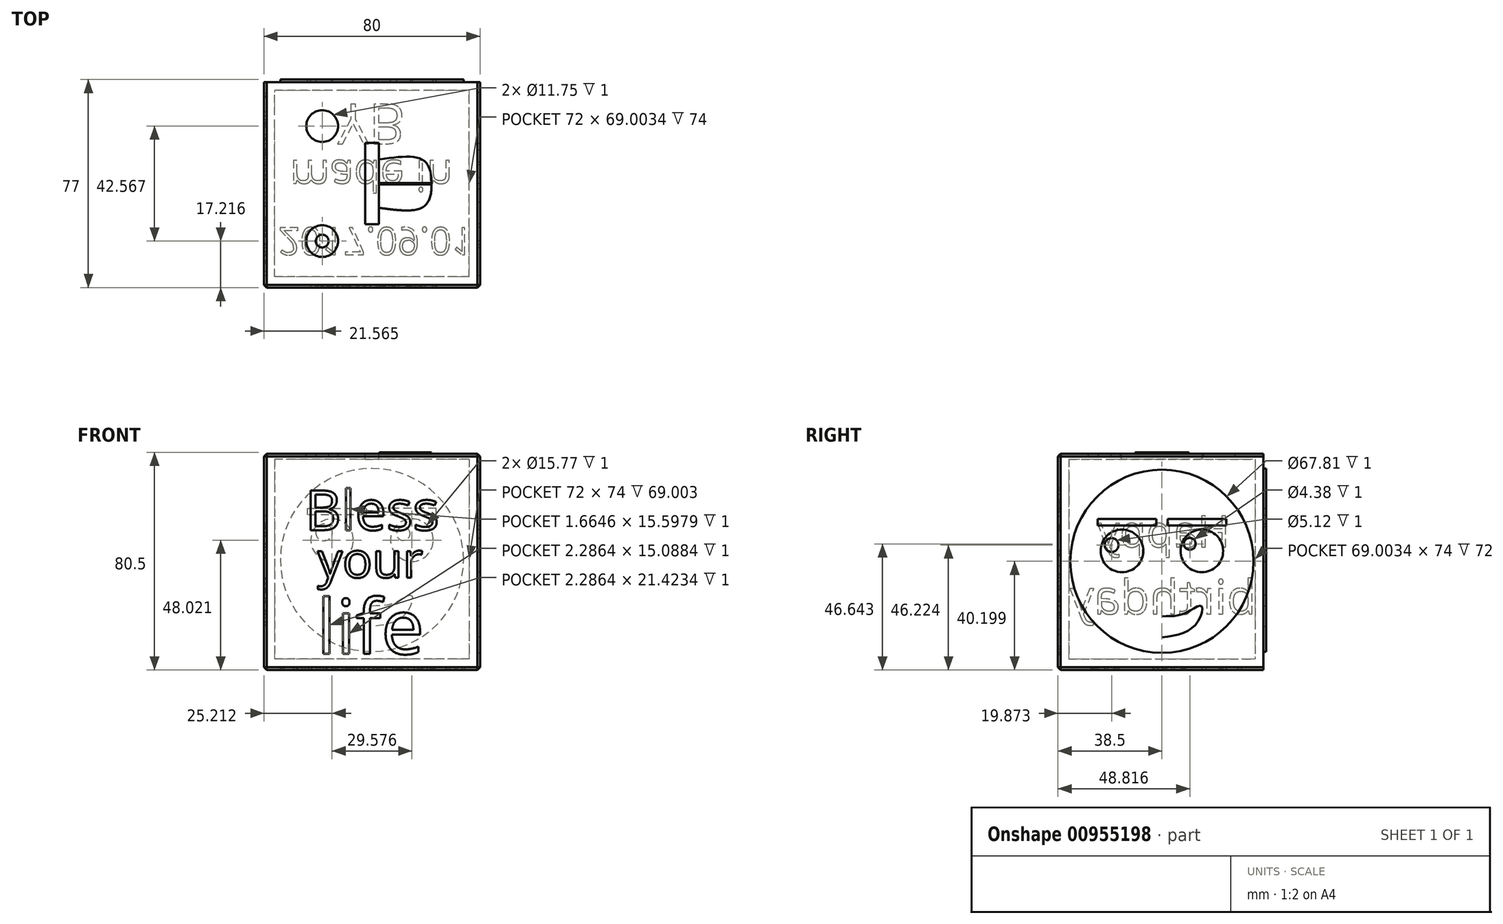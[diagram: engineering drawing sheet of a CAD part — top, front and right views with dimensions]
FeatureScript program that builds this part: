
annotation { "Feature Type Name" : "Feature", "Feature Type Description" : "" }
export const myFeature = defineFeature(function(context is Context, id is Id, definition is map)
    precondition{}
    {
        {
            var Q0;
            Q0=qCreatedBy(makeId("Top.planeOp"),FACE);
            var sketch = newSketch(context, id + "F0", { "sketchPlane" : qUnion([Q0])});
            skLineSegment(sketch, "E0.bottom", {"start": v(40, -38.5) * mm, "end": v(-40, -38.5) * mm});
            skLineSegment(sketch, "E0.top", {"start": v(40, 38.5) * mm, "end": v(-40, 38.5) * mm});
            skLineSegment(sketch, "E0.left", {"start": v(40, -38.5) * mm, "end": v(40, 38.5) * mm});
            skLineSegment(sketch, "E0.right", {"start": v(-40, -38.5) * mm, "end": v(-40, 38.5) * mm});
            skPoint(sketch, "E0.middle", {"position": v(0, 0) * mm});
            skSolve(sketch);
        }
        {
            var Q0;
            Q0 = qSketchRegion(id + "F0", true);
            extrude(context, id + "F1", {"entities" : qUnion([Q0]), "depth" : 78 * mm, "offsetDistance" : 25.4 * mm});
        }
        {
            var Q0;
            Q0=makeQuery(id+"F1.opExtrude","CAP_FACE",FACE,{"disambiguationData":[OSD([sQuery(id+"F0.wireOp",EDGE,"E0.bottom"),sQuery(id+"F0.wireOp",EDGE,"E0.top"),sQuery(id+"F0.wireOp",EDGE,"E0.left"),sQuery(id+"F0.wireOp",EDGE,"E0.right")])],"isStart":false});
            shell(context, id + "F2", {"entities" : qUnion([Q0]), "thickness" : 4 * mm});
        }
        {
            var Q0;
            Q0=makeQuery(id+"F1.opExtrude","CAP_FACE",FACE,{"disambiguationData":[OSD([sQuery(id+"F0.wireOp",EDGE,"E0.bottom"),sQuery(id+"F0.wireOp",EDGE,"E0.top"),sQuery(id+"F0.wireOp",EDGE,"E0.left"),sQuery(id+"F0.wireOp",EDGE,"E0.right")])],"isStart":false});
            var sketch = newSketch(context, id + "F3", { "sketchPlane" : qUnion([Q0])});
            skLineSegment(sketch, "E1.bottom", {"start": v(-40, 38.5) * mm, "end": v(40, 38.5) * mm});
            skLineSegment(sketch, "E1.top", {"start": v(-40, -38.5) * mm, "end": v(40, -38.5) * mm});
            skLineSegment(sketch, "E1.left", {"start": v(-40, 38.5) * mm, "end": v(-40, -38.5) * mm});
            skLineSegment(sketch, "E1.right", {"start": v(40, 38.5) * mm, "end": v(40, -38.5) * mm});
            skPoint(sketch, "E1.middle", {"position": v(0, 0) * mm});
            skSolve(sketch);
        }
        {
            var Q0;
            Q0 = qSketchRegion(id + "F3", true);
            extrude(context, id + "F4", {"entities" : qUnion([Q0]), "operationType" : NewBodyOperationType.ADD, "depth" : 2 * mm, "offsetDistance" : 25.4 * mm});
        }
        {
            var Q0;
            Q0=makeQuery(id+"F4.opExtrude","CAP_FACE",FACE,{"disambiguationData":[OSD([sQuery(id+"F3.wireOp",EDGE,"E1.bottom"),sQuery(id+"F3.wireOp",EDGE,"E1.top"),sQuery(id+"F3.wireOp",EDGE,"E1.left"),sQuery(id+"F3.wireOp",EDGE,"E1.right")])],"isStart":false});
            var sketch = newSketch(context, id + "F5", { "sketchPlane" : qUnion([Q0])});
            skLineSegment(sketch, "E2.bottom", {"start": v(-2.5, 15) * mm, "end": v(2.5, 15) * mm});
            skLineSegment(sketch, "E2.top", {"start": v(-2.5, -15) * mm, "end": v(2.5, -15) * mm});
            skLineSegment(sketch, "E2.left", {"start": v(-2.5, 15) * mm, "end": v(-2.5, -15) * mm});
            skLineSegment(sketch, "E2.right", {"start": v(2.5, 15) * mm, "end": v(2.5, -15) * mm});
            skPoint(sketch, "E2.middle", {"position": v(0, 0) * mm});
            skSolve(sketch);
        }
        {
            var Q0;
            Q0=makeQuery(id+"F5.imprint","IMPRINT",FACE,{"disambiguationData":[TD([[makeQuery(id+"F5.imprint","IMPRINT",EDGE,{"derivedFrom":sQuery(id+"F5.wireOp",EDGE,"E2.bottom")}),-1.0]])]});
            extrude(context, id + "F6", {"entities" : qUnion([Q0]), "operationType" : NewBodyOperationType.REMOVE, "oppositeDirection" : true, "depth" : 25.4 * mm, "offsetDistance" : 25.4 * mm});
        }
        {
            var Q0;
            Q0=makeQuery(id+"F4.opExtrude","CAP_EDGE",EDGE,{"disambiguationData":[OSD([sQuery(id+"F3.wireOp",EDGE,"E1.bottom")])],"isStart":false});
            var Q1;
            Q1=makeQuery(id+"F4.opExtrude","CAP_EDGE",EDGE,{"disambiguationData":[OSD([sQuery(id+"F3.wireOp",EDGE,"E1.right")])],"isStart":false});
            var Q2;
            Q2=makeQuery(id+"F4.boolean.opBoolean","MERGE",EDGE,{"derivedFrom":[makeQuery(id+"F1.opExtrude","SWEPT_EDGE",EDGE,{"disambiguationData":[OSD([sQuery(id+"F0.wireOp",EDGE,"E0.top"),sQuery(id+"F0.wireOp",EDGE,"E0.right")])]}),makeQuery(id+"F4.opExtrude","SWEPT_EDGE",EDGE,{"disambiguationData":[OSD([sQuery(id+"F3.wireOp",EDGE,"E1.bottom"),sQuery(id+"F3.wireOp",EDGE,"E1.left")])]})]});
            var Q3;
            Q3=makeQuery(id+"F4.opExtrude","CAP_EDGE",EDGE,{"disambiguationData":[OSD([sQuery(id+"F3.wireOp",EDGE,"E1.left")])],"isStart":false});
            var Q4;
            Q4=makeQuery(id+"F4.opExtrude","CAP_EDGE",EDGE,{"disambiguationData":[OSD([sQuery(id+"F3.wireOp",EDGE,"E1.top")])],"isStart":false});
            var Q5;
            Q5=makeQuery(id+"F4.boolean.opBoolean","MERGE",EDGE,{"derivedFrom":[makeQuery(id+"F1.opExtrude","SWEPT_EDGE",EDGE,{"disambiguationData":[OSD([sQuery(id+"F0.wireOp",EDGE,"E0.bottom"),sQuery(id+"F0.wireOp",EDGE,"E0.right")])]}),makeQuery(id+"F4.opExtrude","SWEPT_EDGE",EDGE,{"disambiguationData":[OSD([sQuery(id+"F3.wireOp",EDGE,"E1.top"),sQuery(id+"F3.wireOp",EDGE,"E1.left")])]})]});
            var Q6;
            Q6=makeQuery(id+"F1.opExtrude","CAP_EDGE",EDGE,{"disambiguationData":[OSD([sQuery(id+"F0.wireOp",EDGE,"E0.bottom")])],"isStart":true});
            var Q7;
            Q7=makeQuery(id+"F1.opExtrude","CAP_EDGE",EDGE,{"disambiguationData":[OSD([sQuery(id+"F0.wireOp",EDGE,"E0.right")])],"isStart":true});
            var Q8;
            Q8=makeQuery(id+"F4.boolean.opBoolean","MERGE",EDGE,{"derivedFrom":[makeQuery(id+"F1.opExtrude","SWEPT_EDGE",EDGE,{"disambiguationData":[OSD([sQuery(id+"F0.wireOp",EDGE,"E0.bottom"),sQuery(id+"F0.wireOp",EDGE,"E0.left")])]}),makeQuery(id+"F4.opExtrude","SWEPT_EDGE",EDGE,{"disambiguationData":[OSD([sQuery(id+"F3.wireOp",EDGE,"E1.top"),sQuery(id+"F3.wireOp",EDGE,"E1.right")])]})]});
            var Q9;
            Q9=makeQuery(id+"F4.boolean.opBoolean","MERGE",EDGE,{"derivedFrom":[makeQuery(id+"F1.opExtrude","SWEPT_EDGE",EDGE,{"disambiguationData":[OSD([sQuery(id+"F0.wireOp",EDGE,"E0.top"),sQuery(id+"F0.wireOp",EDGE,"E0.left")])]}),makeQuery(id+"F4.opExtrude","SWEPT_EDGE",EDGE,{"disambiguationData":[OSD([sQuery(id+"F3.wireOp",EDGE,"E1.bottom"),sQuery(id+"F3.wireOp",EDGE,"E1.right")])]})]});
            var Q10;
            Q10=makeQuery(id+"F1.opExtrude","CAP_EDGE",EDGE,{"disambiguationData":[OSD([sQuery(id+"F0.wireOp",EDGE,"E0.left")])],"isStart":true});
            var Q11;
            Q11=makeQuery(id+"F1.opExtrude","CAP_FACE",FACE,{"disambiguationData":[OSD([sQuery(id+"F0.wireOp",EDGE,"E0.bottom"),sQuery(id+"F0.wireOp",EDGE,"E0.top"),sQuery(id+"F0.wireOp",EDGE,"E0.left"),sQuery(id+"F0.wireOp",EDGE,"E0.right")])],"isStart":true});
            chamfer(context, id + "F7", {"entities" : qUnion([Q0, Q1, Q2, Q3, Q4, Q5, Q6, Q7, Q8, Q9, Q10, Q11]), "width" : 1 * mm, "tangentPropagation" : true});
        }
        {
            var Q0;
            Q0=makeQuery(id+"F4.boolean.opBoolean","MERGE",FACE,{"derivedFrom":[makeQuery(id+"F1.opExtrude","SWEPT_FACE",FACE,{"disambiguationData":[OSD([sQuery(id+"F0.wireOp",EDGE,"E0.right")])]}),makeQuery(id+"F4.opExtrude","SWEPT_FACE",FACE,{"disambiguationData":[OSD([sQuery(id+"F3.wireOp",EDGE,"E1.left")])]})]});
            var sketch = newSketch(context, id + "F8", { "sketchPlane" : qUnion([Q0])});
            skText(sketch, "E3", { "text": "Happy\n", "fontName": "OpenSans-Regular.ttf"});
            skText(sketch, "E4", { "text": "birthday", "fontName": "OpenSans-Regular.ttf"});
            const initialGuessF8  = {"E3": [-0.02511, 0.0455, 1, 0, 0.01166], "E4": [-0.03482, 0.0207, 1, 0, 0.01267]};
            skSetInitialGuess(sketch, initialGuessF8);
            skSolve(sketch);
        }
        {
            var Q0;
            Q0 = qSketchRegion(id + "F8", true);
            extrude(context, id + "F9", {"entities" : qUnion([Q0]), "operationType" : NewBodyOperationType.REMOVE, "oppositeDirection" : true, "depth" : 1 * mm, "offsetDistance" : 25.4 * mm});
        }
        {
            var Q0;
            Q0=makeQuery(id+"F4.boolean.opBoolean","MERGE",FACE,{"derivedFrom":[makeQuery(id+"F1.opExtrude","SWEPT_FACE",FACE,{"disambiguationData":[OSD([sQuery(id+"F0.wireOp",EDGE,"E0.bottom")])]}),makeQuery(id+"F4.opExtrude","SWEPT_FACE",FACE,{"disambiguationData":[OSD([sQuery(id+"F3.wireOp",EDGE,"E1.top")])]})]});
            var sketch = newSketch(context, id + "F10", { "sketchPlane" : qUnion([Q0])});
            skText(sketch, "E5", { "text": "Bless", "fontName": "OpenSans-Regular.ttf"});
            skText(sketch, "E6", { "text": "your", "fontName": "OpenSans-Regular.ttf"});
            skText(sketch, "E7", { "text": "life", "fontName": "OpenSans-Regular.ttf"});
            const initialGuessF10  = {"E5": [-0.02471, 0.05174, 1, 0, 0.01478], "E6": [-0.02018, 0.03415, 1, 0, 0.0132], "E7": [-0.02038, 0.0059, 1, 0, 0.0203]};
            skSetInitialGuess(sketch, initialGuessF10);
            skSolve(sketch);
        }
        {
            var Q0;
            Q0 = qSketchRegion(id + "F10", true);
            extrude(context, id + "F11", {"entities" : qUnion([Q0]), "operationType" : NewBodyOperationType.REMOVE, "oppositeDirection" : true, "depth" : 1 * mm, "offsetDistance" : 25.4 * mm});
        }
        {
            var Q0;
            Q0=makeQuery(id+"F4.boolean.opBoolean","MERGE",FACE,{"derivedFrom":[makeQuery(id+"F1.opExtrude","SWEPT_FACE",FACE,{"disambiguationData":[OSD([sQuery(id+"F0.wireOp",EDGE,"E0.left")])]}),makeQuery(id+"F4.opExtrude","SWEPT_FACE",FACE,{"disambiguationData":[OSD([sQuery(id+"F3.wireOp",EDGE,"E1.right")])]})]});
            var sketch = newSketch(context, id + "F12", { "sketchPlane" : qUnion([Q0])});
            skCircle(sketch, "E8", {"center": v(0, 40.2) * mm, "radius": 33.9 * mm});
            skSolve(sketch);
        }
        {
            var Q0;
            Q0 = qSketchRegion(id + "F12", true);
            extrude(context, id + "F13", {"entities" : qUnion([Q0]), "operationType" : NewBodyOperationType.REMOVE, "oppositeDirection" : true, "depth" : 1 * mm, "offsetDistance" : 25.4 * mm});
        }
        {
            var Q0;
            Q0=makeQuery(id+"F13.boolean.opBoolean","COPY",FACE,{"derivedFrom":makeQuery(id+"F13.opExtrude","CAP_FACE",FACE,{"disambiguationData":[OSD([sQuery(id+"F12.wireOp",EDGE,"E8")])],"isStart":false})});
            var sketch = newSketch(context, id + "F14", { "sketchPlane" : qUnion([Q0])});
            skLineSegment(sketch, "E9", {"start": v(-23.8, 55.84) * mm, "end": v(-2.12, 55.84) * mm});
            skLineSegment(sketch, "E10", {"start": v(-2.12, 55.84) * mm, "end": v(-2.12, 53.46) * mm});
            skLineSegment(sketch, "E11", {"start": v(-2.12, 53.46) * mm, "end": v(-23.8, 53.46) * mm});
            skLineSegment(sketch, "E12", {"start": v(-23.8, 53.46) * mm, "end": v(-23.8, 55.84) * mm});
            skCircle(sketch, "E13", {"center": v(-14.78, 44.05) * mm, "radius": 7.88 * mm});
            skFitSpline(sketch, "E14", {"points": [v(0, 19.8) * mm, v(-8.09, 20.8) * mm, v(-14.61, 23.64) * mm, v(-12.44, 16.78) * mm, v(0, 12.1) * mm], "startDerivative": vector(-36.85, 3.31) * mm, "endDerivative": vector(49.86, -5.57) * mm});
            skLineSegment(sketch, "E15", {"start": v(0, 85.2) * mm, "end": v(0, -15.17) * mm, "construction": true});
            skLineSegment(sketch, "E16.MirrorCS", {"start": v(2.12, 53.46) * mm, "end": v(23.8, 53.46) * mm});
            skLineSegment(sketch, "E17.MirrorCS", {"start": v(2.12, 55.84) * mm, "end": v(2.12, 53.46) * mm});
            skLineSegment(sketch, "E18.MirrorCS", {"start": v(23.8, 55.84) * mm, "end": v(2.12, 55.84) * mm});
            skLineSegment(sketch, "E19.MirrorCS", {"start": v(23.8, 53.46) * mm, "end": v(23.8, 55.84) * mm});
            skCircle(sketch, "E20.MirrorC", {"center": v(14.78, 44.05) * mm, "radius": 7.88 * mm});
            skFitSpline(sketch, "E21.MirrorCS", {"points": [v(0, 19.8) * mm, v(8.09, 20.8) * mm, v(14.61, 23.64) * mm, v(12.44, 16.78) * mm, v(0, 12.1) * mm], "startDerivative": vector(36.85, 3.31) * mm, "endDerivative": vector(-49.86, -5.57) * mm});
            skSolve(sketch);
        }
        {
            var Q0;
            Q0 = qSketchRegion(id + "F14", true);
            extrude(context, id + "F15", {"entities" : qUnion([Q0]), "operationType" : NewBodyOperationType.ADD, "depth" : 1 * mm, "offsetDistance" : 25.4 * mm});
        }
        {
            var Q0;
            Q0=makeQuery(id+"F15.opExtrude","CAP_FACE",FACE,{"disambiguationData":[OSD([sQuery(id+"F14.wireOp",EDGE,"E13")])],"isStart":false});
            var sketch = newSketch(context, id + "F16", { "sketchPlane" : qUnion([Q0])});
            skCircle(sketch, "E22", {"center": v(-18.63, 46.22) * mm, "radius": 2.56 * mm});
            skCircle(sketch, "E23", {"center": v(10.32, 46.64) * mm, "radius": 2.19 * mm});
            skSolve(sketch);
        }
        {
            var Q0;
            Q0 = qSketchRegion(id + "F16", true);
            extrude(context, id + "F17", {"entities" : qUnion([Q0]), "operationType" : NewBodyOperationType.REMOVE, "oppositeDirection" : true, "depth" : 1 * mm, "offsetDistance" : 25.4 * mm});
        }
        {
            var Q0;
            Q0=makeQuery(id+"F4.boolean.opBoolean","MERGE",FACE,{"derivedFrom":[makeQuery(id+"F1.opExtrude","SWEPT_FACE",FACE,{"disambiguationData":[OSD([sQuery(id+"F0.wireOp",EDGE,"E0.top")])]}),makeQuery(id+"F4.opExtrude","SWEPT_FACE",FACE,{"disambiguationData":[OSD([sQuery(id+"F3.wireOp",EDGE,"E1.bottom")])]})]});
            var sketch = newSketch(context, id + "F18", { "sketchPlane" : qUnion([Q0])});
            skLineSegment(sketch, "E24.bottom", {"start": v(-40, 80) * mm, "end": v(40, 80) * mm});
            skLineSegment(sketch, "E24.top", {"start": v(-40, 0) * mm, "end": v(40, 0) * mm});
            skLineSegment(sketch, "E24.left", {"start": v(-40, 80) * mm, "end": v(-40, 0) * mm});
            skLineSegment(sketch, "E24.right", {"start": v(40, 80) * mm, "end": v(40, 0) * mm});
            skSolve(sketch);
        }
        {
            var Q0;
            Q0 = qSketchRegion(id + "F18", true);
            extrude(context, id + "F19", {"entities" : qUnion([Q0]), "operationType" : NewBodyOperationType.REMOVE, "oppositeDirection" : true, "depth" : 1 * mm, "offsetDistance" : 25.4 * mm});
        }
        {
            var Q0;
            Q0=makeQuery(id+"F19.boolean.opBoolean","COPY",FACE,{"derivedFrom":makeQuery(id+"F19.opExtrude","CAP_FACE",FACE,{"disambiguationData":[OSD([sQuery(id+"F18.wireOp",EDGE,"E24.bottom"),sQuery(id+"F18.wireOp",EDGE,"E24.top"),sQuery(id+"F18.wireOp",EDGE,"E24.left"),sQuery(id+"F18.wireOp",EDGE,"E24.right")])],"isStart":false})});
            var sketch = newSketch(context, id + "F20", { "sketchPlane" : qUnion([Q0])});
            skCircle(sketch, "E25", {"center": v(0, 40.67) * mm, "radius": 33.9 * mm});
            skSolve(sketch);
        }
        {
            var Q0;
            Q0 = qSketchRegion(id + "F20", true);
            extrude(context, id + "F21", {"entities" : qUnion([Q0]), "operationType" : NewBodyOperationType.ADD, "depth" : 1 * mm, "offsetDistance" : 25.4 * mm});
        }
        {
            var Q0;
            Q0=makeQuery(id+"F21.opExtrude","CAP_FACE",FACE,{"disambiguationData":[OSD([sQuery(id+"F20.wireOp",EDGE,"E25")])],"isStart":false});
            var sketch = newSketch(context, id + "F22", { "sketchPlane" : qUnion([Q0])});
            skLineSegment(sketch, "E26", {"start": v(-23.81, 59.82) * mm, "end": v(-2.13, 59.82) * mm});
            skLineSegment(sketch, "E27", {"start": v(-2.13, 59.82) * mm, "end": v(-2.13, 57.43) * mm});
            skLineSegment(sketch, "E28", {"start": v(-2.13, 57.43) * mm, "end": v(-23.81, 57.43) * mm});
            skLineSegment(sketch, "E29", {"start": v(-23.81, 57.43) * mm, "end": v(-23.81, 59.82) * mm});
            skCircle(sketch, "E30", {"center": v(-14.79, 48.02) * mm, "radius": 7.88 * mm});
            skFitSpline(sketch, "E31", {"points": [v(0, 23.76) * mm, v(-8.1, 24.77) * mm, v(-14.62, 27.61) * mm, v(-12.45, 20.75) * mm, v(0, 16.07) * mm], "startDerivative": vector(-36.85, 3.31) * mm, "endDerivative": vector(49.86, -5.57) * mm});
            skLineSegment(sketch, "E32", {"start": v(0, 80.39) * mm, "end": v(0, 0) * mm, "construction": true});
            skLineSegment(sketch, "E33.MirrorCS", {"start": v(2.13, 59.82) * mm, "end": v(2.13, 57.43) * mm});
            skLineSegment(sketch, "E34.MirrorCS", {"start": v(23.81, 59.82) * mm, "end": v(2.13, 59.82) * mm});
            skLineSegment(sketch, "E35.MirrorCS", {"start": v(23.81, 57.43) * mm, "end": v(23.81, 59.82) * mm});
            skLineSegment(sketch, "E36.MirrorCS", {"start": v(2.13, 57.43) * mm, "end": v(23.81, 57.43) * mm});
            skCircle(sketch, "E37.MirrorC", {"center": v(14.79, 48.02) * mm, "radius": 7.88 * mm});
            skFitSpline(sketch, "E38.MirrorCS", {"points": [v(0, 23.76) * mm, v(8.1, 24.77) * mm, v(14.62, 27.61) * mm, v(12.45, 20.75) * mm, v(0, 16.07) * mm], "startDerivative": vector(36.85, 3.31) * mm, "endDerivative": vector(-49.86, -5.57) * mm});
            skSolve(sketch);
        }
        {
            var Q0;
            Q0 = qSketchRegion(id + "F22", true);
            extrude(context, id + "F23", {"entities" : qUnion([Q0]), "operationType" : NewBodyOperationType.REMOVE, "oppositeDirection" : true, "depth" : 1 * mm, "offsetDistance" : 25.4 * mm});
        }
        {
            var Q0;
            Q0=makeQuery(id+"F19.boolean.opBoolean","COPY",FACE,{"derivedFrom":makeQuery(id+"F19.opExtrude","CAP_FACE",FACE,{"disambiguationData":[OSD([sQuery(id+"F18.wireOp",EDGE,"E24.bottom"),sQuery(id+"F18.wireOp",EDGE,"E24.top"),sQuery(id+"F18.wireOp",EDGE,"E24.left"),sQuery(id+"F18.wireOp",EDGE,"E24.right")])],"isStart":false})});
            var sketch = newSketch(context, id + "F24", { "sketchPlane" : qUnion([Q0])});
            skCircle(sketch, "E39", {"center": v(-11.6, 50.42) * mm, "radius": 2.5 * mm});
            skCircle(sketch, "E40", {"center": v(17.76, 50.9) * mm, "radius": 3.1 * mm});
            skSolve(sketch);
        }
        {
            var Q0;
            Q0=makeQuery(id+"F24.imprint","IMPRINT",FACE,{"disambiguationData":[TD([[makeQuery(id+"F24.imprint","IMPRINT",EDGE,{"derivedFrom":sQuery(id+"F24.wireOp",EDGE,"E39")}),1.0]])]});
            var Q1;
            Q1=makeQuery(id+"F24.imprint","IMPRINT",FACE,{"disambiguationData":[TD([[makeQuery(id+"F24.imprint","IMPRINT",EDGE,{"derivedFrom":sQuery(id+"F24.wireOp",EDGE,"E40")}),1.0]])]});
            extrude(context, id + "F25", {"entities" : qUnion([Q0, Q1]), "operationType" : NewBodyOperationType.ADD, "depth" : 1 * mm, "offsetDistance" : 25.4 * mm});
        }
        {
            var Q0;
            Q0=makeQuery(id+"F1.opExtrude","CAP_FACE",FACE,{"disambiguationData":[OSD([sQuery(id+"F0.wireOp",EDGE,"E0.bottom"),sQuery(id+"F0.wireOp",EDGE,"E0.top"),sQuery(id+"F0.wireOp",EDGE,"E0.left"),sQuery(id+"F0.wireOp",EDGE,"E0.right")])],"isStart":true});
            var sketch = newSketch(context, id + "F26", { "sketchPlane" : qUnion([Q0])});
            skText(sketch, "E41", { "text": "2017.09.01", "fontName": "OpenSans-Regular.ttf"});
            skText(sketch, "E42", { "text": "made in", "fontName": "OpenSans-Regular.ttf"});
            skText(sketch, "E43", { "text": "YB", "fontName": "OpenSans-Regular.ttf"});
            const initialGuessF26  = {"E41": [-0.03475, 0.01625, 1, 0, 0.01019], "E42": [-0.0304, -0.00862, 1, 0, 0.01146], "E43": [-0.01278, -0.02946, 1, 0, 0.0149]};
            skSetInitialGuess(sketch, initialGuessF26);
            skSolve(sketch);
        }
        {
            var Q0;
            Q0 = qSketchRegion(id + "F26", true);
            extrude(context, id + "F27", {"entities" : qUnion([Q0]), "operationType" : NewBodyOperationType.REMOVE, "oppositeDirection" : true, "depth" : 1 * mm, "offsetDistance" : 25.4 * mm});
        }
        {
            var Q0;
            Q0=makeQuery(id+"F4.opExtrude","CAP_FACE",FACE,{"disambiguationData":[OSD([sQuery(id+"F3.wireOp",EDGE,"E1.bottom"),sQuery(id+"F3.wireOp",EDGE,"E1.top"),sQuery(id+"F3.wireOp",EDGE,"E1.left"),sQuery(id+"F3.wireOp",EDGE,"E1.right")])],"isStart":false});
            var sketch = newSketch(context, id + "F28", { "sketchPlane" : qUnion([Q0])});
            skCircle(sketch, "E44", {"center": v(-18.43, -21.28) * mm, "radius": 5.88 * mm});
            skLineSegment(sketch, "E45", {"start": v(0, 0) * mm, "end": v(-42.69, 0) * mm, "construction": true});
            skPoint(sketch, "E45.endSnap0", {"position": v(-39, 0) * mm});
            skCircle(sketch, "E46.MirrorC", {"center": v(-18.43, 21.28) * mm, "radius": 5.88 * mm});
            skSolve(sketch);
        }
        {
            var Q0;
            Q0 = qSketchRegion(id + "F28", true);
            extrude(context, id + "F29", {"entities" : qUnion([Q0]), "operationType" : NewBodyOperationType.REMOVE, "oppositeDirection" : true, "depth" : 1 * mm, "offsetDistance" : 25.4 * mm});
        }
        {
            var Q0;
            Q0=makeQuery(id+"F29.boolean.opBoolean","COPY",FACE,{"derivedFrom":makeQuery(id+"F29.opExtrude","CAP_FACE",FACE,{"disambiguationData":[OSD([sQuery(id+"F28.wireOp",EDGE,"E44")])],"isStart":false})});
            var sketch = newSketch(context, id + "F30", { "sketchPlane" : qUnion([Q0])});
            skCircle(sketch, "E47", {"center": v(-18.43, -21.28) * mm, "radius": 2.36 * mm});
            skLineSegment(sketch, "E48", {"start": v(0, 0) * mm, "end": v(-28.82, 0) * mm, "construction": true});
            skCircle(sketch, "E49.MirrorC", {"center": v(-18.43, 21.28) * mm, "radius": 2.36 * mm});
            skSolve(sketch);
        }
        {
            var Q0;
            Q0=makeQuery(id+"F30.imprint","IMPRINT",FACE,{"disambiguationData":[TD([[makeQuery(id+"F30.imprint","IMPRINT",EDGE,{"derivedFrom":sQuery(id+"F30.wireOp",EDGE,"E47")}),1.0]])]});
            var Q1;
            Q1=makeQuery(id+"F30.imprint","IMPRINT",FACE,{"disambiguationData":[TD([[makeQuery(id+"F30.imprint","IMPRINT",EDGE,{"derivedFrom":sQuery(id+"F30.wireOp",EDGE,"E49.MirrorC")}),-1.0]])]});
            extrude(context, id + "F31", {"entities" : qUnion([Q0, Q1]), "operationType" : NewBodyOperationType.ADD, "depth" : 1 * mm, "offsetDistance" : 25.4 * mm});
        }
        {
            var Q0;
            Q0=makeQuery(id+"F4.opExtrude","CAP_FACE",FACE,{"disambiguationData":[OSD([sQuery(id+"F3.wireOp",EDGE,"E1.bottom"),sQuery(id+"F3.wireOp",EDGE,"E1.top"),sQuery(id+"F3.wireOp",EDGE,"E1.left"),sQuery(id+"F3.wireOp",EDGE,"E1.right")])],"isStart":false});
            var sketch = newSketch(context, id + "F32", { "sketchPlane" : qUnion([Q0])});
            skFitSpline(sketch, "E50", {"points": [v(2.5, -8.95) * mm, v(18.6, -8.85) * mm, v(21.79, -3.78) * mm, v(21.98, 0) * mm], "startDerivative": vector(40.28, -5.54) * mm, "endDerivative": vector(-0.49, 15.31) * mm});
            skFitSpline(sketch, "E51.MirrorCS", {"points": [v(2.5, 8.95) * mm, v(18.6, 8.85) * mm, v(21.79, 3.78) * mm, v(21.98, 0) * mm], "startDerivative": vector(40.28, 5.54) * mm, "endDerivative": vector(-0.49, -15.31) * mm});
            skLineSegment(sketch, "E52", {"start": v(2.5, -8.95) * mm, "end": v(2.5, 8.95) * mm});
            skSolve(sketch);
        }
        {
            var Q0;
            Q0 = qSketchRegion(id + "F32", true);
            extrude(context, id + "F33", {"entities" : qUnion([Q0]), "operationType" : NewBodyOperationType.ADD, "depth" : 0.5 * mm, "offsetDistance" : 25.4 * mm});
        }
        {
            var Q0;
            Q0=makeQuery(id+"F33.opExtrude","CAP_EDGE",EDGE,{"disambiguationData":[OSD([sQuery(id+"F32.wireOp",EDGE,"E52")])],"isStart":false});
            fillet(context, id + "F34", {"entities" : qUnion([Q0]), "radius" : 0.5 * mm, "tangentPropagation" : true, "allowEdgeOverflow" : false});
        }
        {
            var Q0;
            Q0=makeQuery(id+"F33.opExtrude","CAP_FACE",FACE,{"disambiguationData":[OSD([sQuery(id+"F32.wireOp",EDGE,"E50"),sQuery(id+"F32.wireOp",EDGE,"E51.MirrorCS"),sQuery(id+"F32.wireOp",EDGE,"E52")])],"isStart":false});
            var sketch = newSketch(context, id + "F35", { "sketchPlane" : qUnion([Q0])});
            skLineSegment(sketch, "E53.bottom", {"start": v(3, -0.25) * mm, "end": v(21.98, -0.25) * mm});
            skLineSegment(sketch, "E53.top", {"start": v(3, 0) * mm, "end": v(21.98, 0) * mm});
            skLineSegment(sketch, "E53.left", {"start": v(3, -0.25) * mm, "end": v(3, 0) * mm});
            skLineSegment(sketch, "E53.right", {"start": v(21.98, -0.25) * mm, "end": v(21.98, 0) * mm});
            skLineSegment(sketch, "E54.bottom", {"start": v(3, 0) * mm, "end": v(3, 0) * mm});
            skLineSegment(sketch, "E54.top", {"start": v(3, 0.25) * mm, "end": v(3, 0.25) * mm});
            skLineSegment(sketch, "E54.left", {"start": v(3, 0) * mm, "end": v(3, 0.25) * mm});
            skLineSegment(sketch, "E54.right", {"start": v(3, 0) * mm, "end": v(3, 0.25) * mm});
            skLineSegment(sketch, "E55", {"start": v(3, 0.25) * mm, "end": v(22, 0.25) * mm});
            skLineSegment(sketch, "E56", {"start": v(22, 0.25) * mm, "end": v(21.98, 0) * mm});
            skSolve(sketch);
        }
        {
            var Q0;
            Q0 = qSketchRegion(id + "F35", true);
            extrude(context, id + "F36", {"entities" : qUnion([Q0]), "operationType" : NewBodyOperationType.REMOVE, "oppositeDirection" : true, "depth" : 0.1 * mm, "offsetDistance" : 25.4 * mm});
        }
    });
